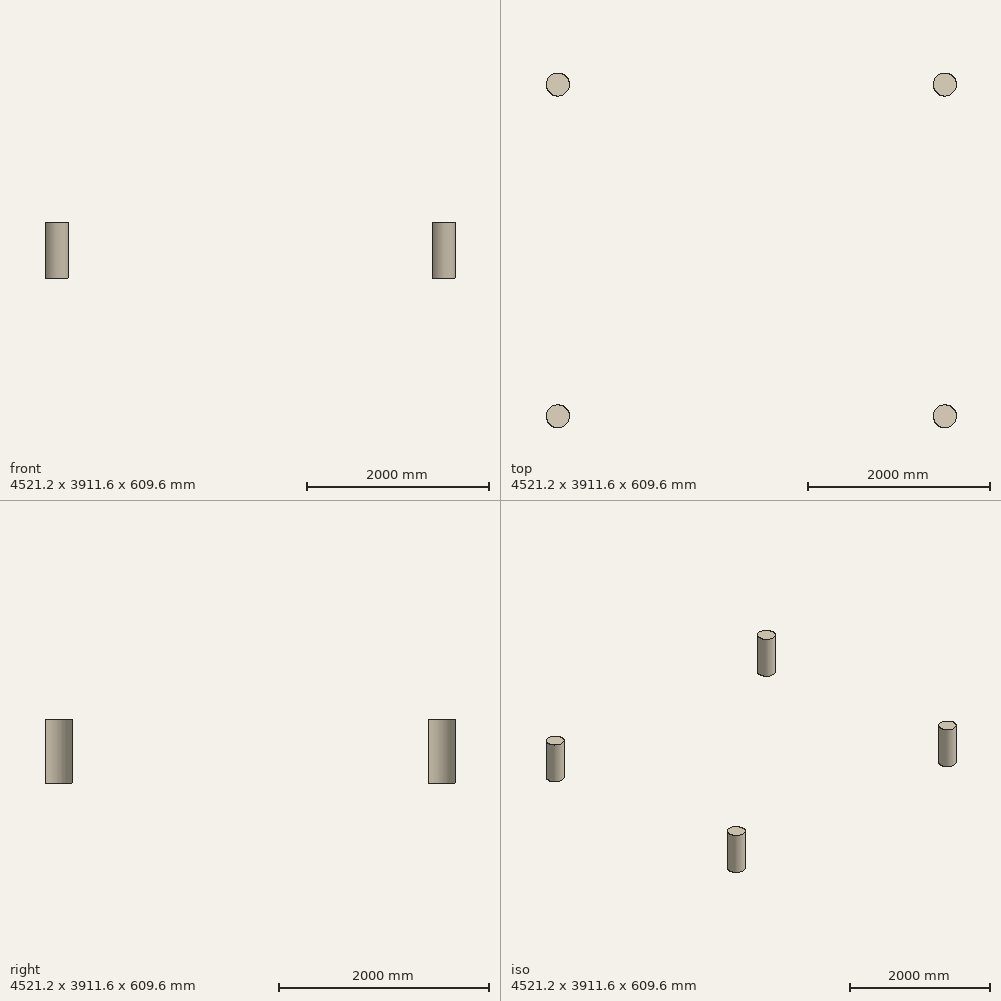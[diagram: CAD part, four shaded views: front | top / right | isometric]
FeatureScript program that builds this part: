
annotation { "Feature Type Name" : "Feature", "Feature Type Description" : "" }
export const myFeature = defineFeature(function(context is Context, id is Id, definition is map)
    precondition{}
    {
        {
            var Q0;
            Q0=qCreatedBy(makeId("Top.planeOp"),FACE);
            var sketch = newSketch(context, id + "F0", { "sketchPlane" : qUnion([Q0])});
            skCircle(sketch, "E0", {"center": v(-2133.6, 1828.8) * mm, "radius": 127 * mm});
            skCircle(sketch, "E1", {"center": v(2133.6, 1828.8) * mm, "radius": 127 * mm});
            skCircle(sketch, "E2", {"center": v(2133.6, -1828.8) * mm, "radius": 127 * mm});
            skCircle(sketch, "E3", {"center": v(-2133.6, -1828.8) * mm, "radius": 127 * mm});
            skSolve(sketch);
        }
        {
            var Q0;
            Q0=makeQuery(id+"F0.imprint","IMPRINT",FACE,{"disambiguationData":[TD([[makeQuery(id+"F0.imprint","IMPRINT",EDGE,{"derivedFrom":sQuery(id+"F0.wireOp",EDGE,"E0")}),1.0]])]});
            var Q1;
            Q1=makeQuery(id+"F0.imprint","IMPRINT",FACE,{"disambiguationData":[TD([[makeQuery(id+"F0.imprint","IMPRINT",EDGE,{"derivedFrom":sQuery(id+"F0.wireOp",EDGE,"E1")}),1.0]])]});
            var Q2;
            Q2=makeQuery(id+"F0.imprint","IMPRINT",FACE,{"disambiguationData":[TD([[makeQuery(id+"F0.imprint","IMPRINT",EDGE,{"derivedFrom":sQuery(id+"F0.wireOp",EDGE,"E2")}),1.0]])]});
            var Q3;
            Q3=makeQuery(id+"F0.imprint","IMPRINT",FACE,{"disambiguationData":[TD([[makeQuery(id+"F0.imprint","IMPRINT",EDGE,{"derivedFrom":sQuery(id+"F0.wireOp",EDGE,"E3")}),1.0]])]});
            extrude(context, id + "F1", {"entities" : qUnion([Q0, Q1, Q2, Q3]), "oppositeDirection" : true, "depth" : 609.6 * mm});
        }
    });
